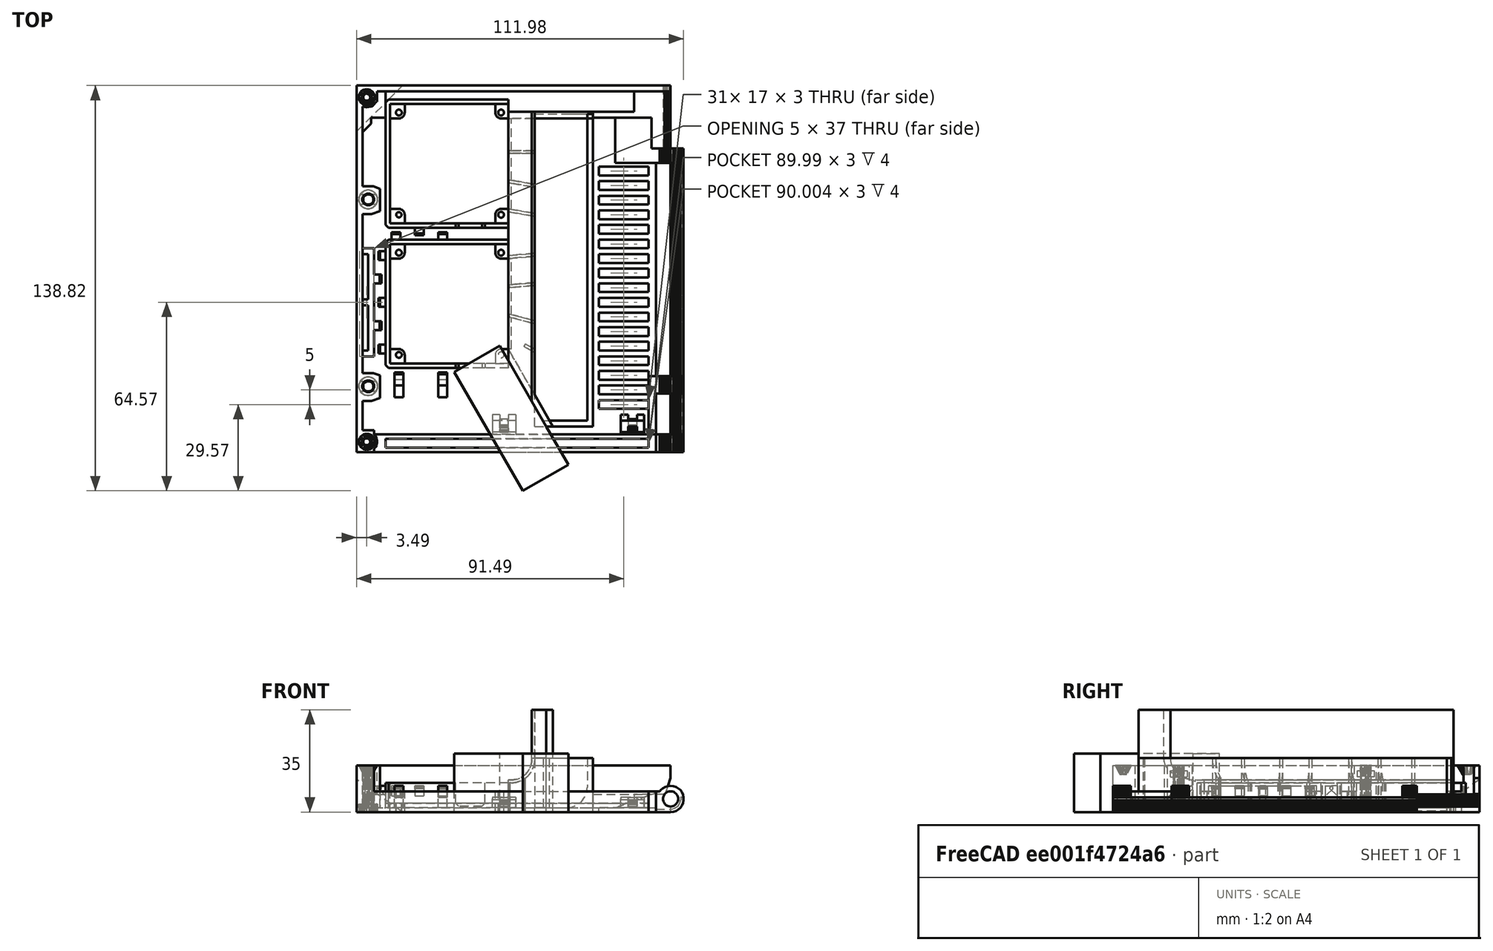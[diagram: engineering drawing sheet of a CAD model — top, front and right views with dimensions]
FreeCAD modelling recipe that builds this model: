
FCSTD DOCUMENT  (FreeCAD 0.18R14555 (Git shallow))
Label: SKR-DOOR-FROM-TOP
License: All rights reserved
LicenseURL: http://en.wikipedia.org/wiki/All_rights_reserved
objects: Part::Box×52, Part::MultiFuse×22, Part::Cut×21, Part::Feature×20, Part::Cylinder×8, Part::Chamfer×6, Part::Fillet×2, Mesh::Feature×1, Part::MultiCommon×1
note: 132 computed .brp shape members not serialized (recipe doc carries the construction recipe); baked Part::Feature solids carry a one-line shape summary decoded from their .brp

FEATURE [Mesh::Feature] SKR_13_DOOR_1_  label="SKR_13_DOOR(1)"
FEATURE [Part::Feature] Fusion001
  shape: bbox 112 x 125.5 x 16 mm, 668 faces (baked)
FEATURE [Part::Feature] Cut001_solid  label="4010-blower"
  Placement = pos=(-24,-12,0) rot=(0,0,1;3.14159rad)
  shape: bbox 42 x 44 x 10 mm, 38 faces (baked)
FEATURE [Part::Feature] Cut001_solid001  label="4010-blower001"
  Placement = pos=(-24,36,0) rot=(0,0,1;3.14159rad)
  shape: bbox 42 x 44 x 10 mm, 38 faces (baked)
FEATURE [Part::Box] Box002  label="Cube002"
  AttacherType = Attacher::AttachEngine3D
  Height = 10
  Length = 42
  Placement = pos=(-46,-6,0) rot=(0,0,1;0rad)
  Width = 44
FEATURE [Part::Box] Box003  label="Cube003"
  AttacherType = Attacher::AttachEngine3D
  Height = 10
  Length = 42
  Placement = pos=(-46,-54,0) rot=(0,0,1;0rad)
  Width = 44
FEATURE [Part::Chamfer] Chamfer
  Base = -> Box003
  Edges = 2 edges r=1.2: [Edge1,Edge3]
  Placement = pos=(0,20,0) rot=(0,0,1;0rad)
FEATURE [Part::Chamfer] Chamfer001
  Base = -> Box002
  Edges = 2 edges r=1.2: [Edge1,Edge3]
  Placement = pos=(0,20,0) rot=(0,0,1;0rad)
FEATURE [Part::Feature] Part__Feature  label="wire-mounter"
  Placement = pos=(-24,-80,64.25) rot=(-1,0,0;1.5708rad)
  shape: bbox 8 x 9.5 x 3.5 mm, 30 faces (baked)
FEATURE [Part::Feature] Part__Feature002  label="wire-mounter002"
  Placement = pos=(20,-80,64.25) rot=(-1,0,0;1.5708rad)
  shape: bbox 8 x 9.5 x 3.5 mm, 30 faces (baked)
FEATURE [Part::Feature] Chamfer003001  label="Chamfer004"
  Placement = pos=(-28,9,0) rot=(0,0,1;0rad)
  shape: bbox 3 x 3.5 x 4 mm, 8 faces (baked)
FEATURE [Part::Feature] Chamfer003002  label="Chamfer005"
  Placement = pos=(-44,9,0) rot=(0,0,1;0rad)
  shape: bbox 3 x 3.5 x 4 mm, 8 faces (baked)
FEATURE [Part::Feature] Chamfer003003  label="Chamfer006"
  Placement = pos=(-33,15,0) rot=(0,0,1;3.14159rad)
  shape: bbox 3 x 3.5 x 4 mm, 8 faces (baked)
FEATURE [Part::MultiFuse] Fusion002
  Shapes = -> [Cut001_solid001,Chamfer003003]
FEATURE [Part::MultiFuse] Fusion003
  Shapes = -> [Cut001_solid,Chamfer003001]
FEATURE [Part::MultiFuse] Fusion004
  Shapes = -> [Fusion003,Chamfer003002]
FEATURE [Part::Cut] Cut
  Base = -> Fusion001
  Tool = -> Chamfer001
FEATURE [Part::Cut] Cut001
  Base = -> Cut
  Tool = -> Chamfer
FEATURE [Part::Box] Box005  label="Cube005"
  AttacherType = Attacher::AttachEngine3D
  Height = 9
  Length = 2
  Placement = pos=(-52,-30,0) rot=(0,0,1;0rad)
  Width = 37
FEATURE [Part::Feature] Chamfer003005  label="wire-clip002"
  Placement = pos=(-45,-13,0) rot=(0,0,1;1.5708rad)
  shape: bbox 3.5 x 3 x 4 mm, 8 faces (baked)
FEATURE [Part::Feature] Chamfer003006  label="wire-clip003"
  Placement = pos=(-51,-2,0) rot=(0,0,-1;1.5708rad)
  shape: bbox 3.5 x 3 x 4 mm, 8 faces (baked)
FEATURE [Part::Feature] Chamfer003007  label="wire-clip004"
  Placement = pos=(-51,-18,0) rot=(0,0,-1;1.5708rad)
  shape: bbox 3.5 x 3 x 4 mm, 8 faces (baked)
FEATURE [Part::Feature] Chamfer003008  label="wire-clip005"
  Placement = pos=(-45,-29,0) rot=(0,0,1;1.5708rad)
  shape: bbox 3.5 x 3 x 4 mm, 8 faces (baked)
FEATURE [Part::Feature] Chamfer003009  label="wire-clip006"
  Placement = pos=(-45,3,0) rot=(0,0,1;1.5708rad)
  shape: bbox 3.5 x 3 x 4 mm, 8 faces (baked)
FEATURE [Part::Box] Box006  label="Cube006"
  AttacherType = Attacher::AttachEngine3D
  Height = 9
  Length = 4
  Placement = pos=(-55,-30,0) rot=(0,0,1;0rad)
  Width = 2
FEATURE [Part::Box] Box007  label="Cube007"
  AttacherType = Attacher::AttachEngine3D
  Height = 9
  Length = 4
  Placement = pos=(-55,5,0) rot=(0,0,1;0rad)
  Width = 2
FEATURE [Part::Box] Box008  label="Cube008"
  AttacherType = Attacher::AttachEngine3D
  Height = 9
  Length = 4
  Placement = pos=(-55,-12.5,0) rot=(0,0,1;0rad)
  Width = 2
FEATURE [Part::MultiFuse] Fusion006
  Shapes = -> [Fusion004,Chamfer003009,Chamfer003005,Chamfer003008]
FEATURE [Part::Box] Box009  label="Cube009"
  AttacherType = Attacher::AttachEngine3D
  Height = 9
  Length = 3
  Placement = pos=(-43,-40,0) rot=(0,0,1;0rad)
  Width = 2
FEATURE [Part::Box] Box010  label="Cube010"
  AttacherType = Attacher::AttachEngine3D
  Height = 9
  Length = 3
  Placement = pos=(-12,-40,0) rot=(0,0,1;0rad)
  Width = 2
FEATURE [Part::Feature] Chamfer003010  label="wire-clip007"
  Placement = pos=(-43,-39,0) rot=(0,0,1;0rad)
  shape: bbox 3 x 3.5 x 4 mm, 8 faces (baked)
FEATURE [Part::Feature] Chamfer003011  label="wire-clip008"
  Placement = pos=(-12,-39,0) rot=(0,0,1;0rad)
  shape: bbox 3 x 3.5 x 4 mm, 8 faces (baked)
FEATURE [Part::Box] Box011  label="Cube011"
  AttacherType = Attacher::AttachEngine3D
  Height = 9
  Length = 3
  Placement = pos=(-43,-44,0) rot=(0,0,1;0rad)
  Width = 6
FEATURE [Part::Box] Box012  label="Cube012"
  AttacherType = Attacher::AttachEngine3D
  Height = 9
  Length = 3
  Placement = pos=(-36,-44,0) rot=(0,0,1;0rad)
  Width = 6
FEATURE [Part::Chamfer] Chamfer003014
  Base = -> Box011
  Edges = 1 edges r=4: [Edge10]
FEATURE [Part::Chamfer] Chamfer003015
  Base = -> Box012
  Edges = 1 edges r=4: [Edge10]
  Placement = pos=(24,0,0) rot=(0,0,1;0rad)
FEATURE [Part::MultiFuse] Fusion007
  Shapes = -> [Box007,Box005,Box006,Box008,Chamfer003006,Chamfer003007]
FEATURE [Part::MultiFuse] Fusion008
  Shapes = -> [Chamfer003014,Chamfer003010,Box009]
FEATURE [Part::MultiFuse] Fusion009
  Placement = pos=(-16,0,0) rot=(0,0,1;0rad)
  Shapes = -> [Box010,Chamfer003011,Chamfer003015]
FEATURE [Part::MultiFuse] Fusion010
  Shapes = -> [Cut001,Fusion007]
FEATURE [Part::MultiFuse] Fusion011
  Shapes = -> [Fusion010,Fusion009]
FEATURE [Part::MultiFuse] Fusion012
  Shapes = -> [Fusion011,Fusion008]
FEATURE [Part::Cylinder] Cylinder  label="screw-hole-1"
  Angle = 360
  AttacherType = Attacher::AttachEngine3D
  Height = 10
  Placement = pos=(-41.5,5.5,0) rot=(0,0,1;0rad)
  Radius = 1
FEATURE [Part::Cylinder] Cylinder001  label="screw-hole-2"
  Angle = 360
  AttacherType = Attacher::AttachEngine3D
  Height = 10
  Placement = pos=(-41.5,18.5,0) rot=(0,0,1;0rad)
  Radius = 0.9
FEATURE [Part::Cylinder] Cylinder002  label="screw-hole-003"
  Angle = 360
  AttacherType = Attacher::AttachEngine3D
  Height = 10
  Placement = pos=(-6.5,-29.5,0) rot=(0,0,1;0rad)
  Radius = 1
FEATURE [Part::Cylinder] Cylinder003  label="screw-hole-004"
  Angle = 360
  AttacherType = Attacher::AttachEngine3D
  Height = 10
  Placement = pos=(-41.5,53.5,0) rot=(0,0,1;0rad)
  Radius = 1
FEATURE [Part::Cylinder] Cylinder004  label="screw-hole-005"
  Angle = 360
  AttacherType = Attacher::AttachEngine3D
  Height = 10
  Placement = pos=(-6.5,5.5,0) rot=(0,0,1;0rad)
  Radius = 1
FEATURE [Part::Cylinder] Cylinder005  label="screw-hole-006"
  Angle = 360
  AttacherType = Attacher::AttachEngine3D
  Height = 10
  Placement = pos=(-6.5,53.5,0) rot=(0,0,1;0rad)
  Radius = 1
FEATURE [Part::Cylinder] Cylinder006  label="screw-hole-007"
  Angle = 360
  AttacherType = Attacher::AttachEngine3D
  Height = 10
  Placement = pos=(-41.5,-29.5,0) rot=(0,0,1;0rad)
  Radius = 1
FEATURE [Part::Cylinder] Cylinder007  label="screw-hole-008"
  Angle = 360
  AttacherType = Attacher::AttachEngine3D
  Height = 10
  Placement = pos=(-6.5,18.5,0) rot=(0,0,1;0rad)
  Radius = 1
FEATURE [Part::Cut] Cut002
  Base = -> Fusion002
  Tool = -> Cylinder001
FEATURE [Part::Cut] Cut003
  Base = -> Cut002
  Tool = -> Cylinder007
FEATURE [Part::Cut] Cut004
  Base = -> Cut003
  Tool = -> Cylinder003
FEATURE [Part::Cut] Cut005
  Base = -> Cut004
  Tool = -> Cylinder005
FEATURE [Part::Cut] Cut006
  Base = -> Fusion006
  Tool = -> Cylinder006
FEATURE [Part::Cut] Cut007
  Base = -> Cut006
  Tool = -> Cylinder002
FEATURE [Part::Cut] Cut008
  Base = -> Cut007
  Tool = -> Cylinder
FEATURE [Part::Cut] Cut009
  Base = -> Cut008
  Tool = -> Cylinder004
FEATURE [Part::MultiFuse] Fusion013
  Shapes = -> [Fusion012,Cut009]
FEATURE [Part::MultiFuse] Fusion014  label="dorr-base"
  Shapes = -> [Cut005,Fusion013]
FEATURE [Part::Box] Box052  label="Cube050"
  AttacherType = Attacher::AttachEngine3D
  Height = 35
  Length = 14
  Placement = pos=(-5.75882,-15.9659,0) rot=(0,0,-1;0.261799rad)
  Width = 1
FEATURE [Part::Box] Box053  label="Cube051"
  AttacherType = Attacher::AttachEngine3D
  Height = 35
  Length = 36
  Placement = pos=(-6.99679,-26.3636,0) rot=(0,0,-1;1.0472rad)
  Width = 2
FEATURE [Part::Box] Box081  label="Cube079"
  AttacherType = Attacher::AttachEngine3D
  Height = 10
  Length = 17
  Placement = pos=(30,-43,0) rot=(0,0,1;0rad)
  Width = 3
FEATURE [Part::Box] Box082  label="Cube080"
  AttacherType = Attacher::AttachEngine3D
  Height = 10
  Length = 17
  Placement = pos=(30,-38,0) rot=(0,0,1;0rad)
  Width = 3
FEATURE [Part::Box] Box083  label="Cube081"
  AttacherType = Attacher::AttachEngine3D
  Height = 10
  Length = 17
  Placement = pos=(30,-28,0) rot=(0,0,1;0rad)
  Width = 3
FEATURE [Part::Box] Box084  label="Cube082"
  AttacherType = Attacher::AttachEngine3D
  Height = 10
  Length = 17
  Placement = pos=(30,-33,0) rot=(0,0,1;0rad)
  Width = 3
FEATURE [Part::Box] Box085  label="Cube083"
  AttacherType = Attacher::AttachEngine3D
  Height = 10
  Length = 17
  Placement = pos=(30,-23,0) rot=(0,0,1;0rad)
  Width = 3
FEATURE [Part::Box] Box086  label="Cube084"
  AttacherType = Attacher::AttachEngine3D
  Height = 10
  Length = 17
  Placement = pos=(30,-18,0) rot=(0,0,1;0rad)
  Width = 3
FEATURE [Part::Box] Box087  label="Cube085"
  AttacherType = Attacher::AttachEngine3D
  Height = 10
  Length = 17
  Placement = pos=(30,-13,0) rot=(0,0,1;0rad)
  Width = 3
FEATURE [Part::Box] Box088  label="Cube086"
  AttacherType = Attacher::AttachEngine3D
  Height = 10
  Length = 17
  Placement = pos=(30,-8,0) rot=(0,0,1;0rad)
  Width = 3
FEATURE [Part::Box] Box089  label="Cube087"
  AttacherType = Attacher::AttachEngine3D
  Height = 10
  Length = 17
  Placement = pos=(30,-3,0) rot=(0,0,1;0rad)
  Width = 3
FEATURE [Part::Box] Box090  label="Cube088"
  AttacherType = Attacher::AttachEngine3D
  Height = 10
  Length = 17
  Placement = pos=(30,2,0) rot=(0,0,1;0rad)
  Width = 3
FEATURE [Part::Box] Box091  label="Cube089"
  AttacherType = Attacher::AttachEngine3D
  Height = 10
  Length = 17
  Placement = pos=(30,7,0) rot=(0,0,1;0rad)
  Width = 3
FEATURE [Part::Box] Box092  label="Cube090"
  AttacherType = Attacher::AttachEngine3D
  Height = 10
  Length = 17
  Placement = pos=(30,12,0) rot=(0,0,1;0rad)
  Width = 3
FEATURE [Part::Box] Box093  label="Cube091"
  AttacherType = Attacher::AttachEngine3D
  Height = 10
  Length = 17
  Placement = pos=(30,17,0) rot=(0,0,1;0rad)
  Width = 3
FEATURE [Part::Box] Box094  label="Cube092"
  AttacherType = Attacher::AttachEngine3D
  Height = 10
  Length = 17
  Placement = pos=(30,27,0) rot=(0,0,1;0rad)
  Width = 3
FEATURE [Part::Box] Box095  label="Cube093"
  AttacherType = Attacher::AttachEngine3D
  Height = 10
  Length = 17
  Placement = pos=(30,22,0) rot=(0,0,1;0rad)
  Width = 3
FEATURE [Part::Box] Box096  label="Cube094"
  AttacherType = Attacher::AttachEngine3D
  Height = 10
  Length = 17
  Placement = pos=(30,32,0) rot=(0,0,1;0rad)
  Width = 3
FEATURE [Part::Box] Box098  label="trim-a001"
  AttacherType = Attacher::AttachEngine3D
  Height = 38
  Length = 35
  Placement = pos=(-20.8532,-34.3636,0) rot=(0,0,-1;1.0472rad)
  Width = 16
FEATURE [Part::Box] Box099  label="Cube095"
  AttacherType = Attacher::AttachEngine3D
  Height = 35
  Length = 10
  Placement = pos=(1.36603,-26.634,0) rot=(0,0,-1;0.523599rad)
  Width = 1
FEATURE [Part::Box] Box100  label="Cube096"
  AttacherType = Attacher::AttachEngine3D
  Height = 35
  Length = 13
  Placement = pos=(-5.49429,3.36927,0) rot=(0,0,1;0.087266rad)
  Width = 1
FEATURE [Part::Box] Box101  label="Cube097"
  AttacherType = Attacher::AttachEngine3D
  Height = 35
  Length = 15
  Placement = pos=(-5.72341,19.8039,0) rot=(0,0,-1;0.174533rad)
  Width = 1
FEATURE [Part::Box] Box102  label="Cube098"
  AttacherType = Attacher::AttachEngine3D
  Height = 35
  Length = 16
  Placement = pos=(-6.24144,-6.6961,0) rot=(0,0,1;0.087266rad)
  Width = 1
FEATURE [Part::Box] Box103  label="Cube099"
  AttacherType = Attacher::AttachEngine3D
  Height = 35
  Length = 13
  Placement = pos=(-4.73861,29.6302,0) rot=(0,0,-1;0.174533rad)
  Width = 1
FEATURE [Part::Box] Box104  label="Cube100"
  AttacherType = Attacher::AttachEngine3D
  Height = 35
  Length = 10
  Placement = pos=(-4,39.5,0) rot=(0,0,1;0rad)
  Width = 1
FEATURE [Part::Box] Box105  label="Cube101"
  AttacherType = Attacher::AttachEngine3D
  Height = 35
  Length = 40
  Placement = pos=(-4,51.5,0) rot=(0,0,1;0rad)
  Width = 2.25
FEATURE [Part::Box] Box107  label="Cube103"
  AttacherType = Attacher::AttachEngine3D
  Height = 43
  Length = 10
  Placement = pos=(5,-41,0) rot=(0,0,1;0rad)
  Width = 92
FEATURE [Part::Box] Box108  label="trim-a002"
  AttacherType = Attacher::AttachEngine3D
  Height = 20
  Length = 47
  Placement = pos=(-22.5852,-35.3636,0) rot=(0,0,-1;1.0472rad)
  Width = 18
FEATURE [Part::Box] Box111  label="Cube106"
  AttacherType = Attacher::AttachEngine3D
  Height = 10
  Length = 17
  Placement = pos=(30,-48,0) rot=(0,0,1;0rad)
  Width = 3
FEATURE [Part::Chamfer] Chamfer003019
  Base = -> Fusion014
  Edges = 2 edges r=1: [Edge106,Edge143]
FEATURE [Part::MultiFuse] Fusion018010
  Shapes = -> [Box053,Box052,Box101,Box103,Box100,Box102,Box104,Box105,Box099]
FEATURE [Part::Cut] Cut019
  Base = -> Fusion018010
  Tool = -> Box107
FEATURE [Part::Box] Box112  label="Cube107"
  AttacherType = Attacher::AttachEngine3D
  Height = 40
  Length = 10
  Placement = pos=(-14,-34,0) rot=(0,0,1;0rad)
  Width = 120
FEATURE [Part::Cut] Cut020
  Base = -> Cut019
  Tool = -> Box112
FEATURE [Part::Chamfer] Chamfer003020
  Base = -> Cut020
  Edges = 4 edges r=0.5: [Edge16,Edge40,Edge64,Edge75]
FEATURE [Part::Box] Box114  label="Cube109"
  AttacherType = Attacher::AttachEngine3D
  Height = 30
  Length = 9
  Placement = pos=(-4,-54,10) rot=(0,0,1;0rad)
  Width = 107.75
FEATURE [Part::Feature] Fillet002002001  label="Fillet002003"
  shape: bbox 9 x 107.8 x 25 mm, 10 faces (baked)
FEATURE [Part::Fillet] Fillet002002002
  Base = -> Box114
  Edges = 1 edges r=7: [Edge8]
  Placement = pos=(0,0,1) rot=(0,0,1;0rad)
FEATURE [Part::Cut] Cut022
  Base = -> Fillet002002001
  Tool = -> Box098
FEATURE [Part::Box] Box116  label="Cube111"
  AttacherType = Attacher::AttachEngine3D
  Height = 1.5
  Length = 20
  Placement = pos=(5,-54,0) rot=(0,0,1;0rad)
  Width = 107
FEATURE [Part::Box] Box117  label="Cube112"
  AttacherType = Attacher::AttachEngine3D
  Height = 18.5
  Length = 2
  Placement = pos=(23,-54,0) rot=(0,0,1;0rad)
  Width = 107
FEATURE [Part::MultiFuse] Fusion018011
  Shapes = -> [Box116,Box117]
FEATURE [Part::Fillet] Fillet002002003
  Base = -> Fusion018011
  Edges = 1 edges r=7: [Edge9]
FEATURE [Part::Box] Box118  label="Cube113"
  AttacherType = Attacher::AttachEngine3D
  Height = 41
  Length = 16
  Placement = pos=(0,-64,0) rot=(0,0,1;0rad)
  Width = 10
FEATURE [Part::Box] Box119  label="Cube114"
  AttacherType = Attacher::AttachEngine3D
  Height = 18.5
  Length = 17
  Placement = pos=(8,-54,0) rot=(0,0,1;0rad)
  Width = 2
FEATURE [Part::Cut] Cut025
  Base = -> Box119
  Tool = -> Box108
FEATURE [Part::MultiFuse] Fusion018012
  Shapes = -> [Cut025,Fillet002002003]
FEATURE [Part::Box] Box120  label="Cube115"
  AttacherType = Attacher::AttachEngine3D
  Height = 38
  Length = 14
  Placement = pos=(25,46,0) rot=(0,0,1;0rad)
  Width = 14
FEATURE [Part::Box] Box121  label="trim-a003"
  AttacherType = Attacher::AttachEngine3D
  Height = 20
  Length = 47
  Placement = pos=(-22.5852,-35.3636,0) rot=(0,0,-1;1.0472rad)
  Width = 18
FEATURE [Part::Box] Box122  label="Cube116"
  AttacherType = Attacher::AttachEngine3D
  Height = 19
  Length = 23
  Placement = pos=(5,45,18.5) rot=(0,0,1;0rad)
  Width = 14
FEATURE [Part::MultiFuse] Fusion018013
  Placement = pos=(-3,0,0) rot=(0,0,1;0rad)
  Shapes = -> [Box111,Box086,Box085,Box083,Box088,Box087,Box081,Box092,Box093,Box082,Box094,Box084,Box089,Box091,Box090,Box096,Box095]
FEATURE [Part::Cut] Cut028
  Base = -> Chamfer003019
  Tool = -> Fusion018013
FEATURE [Part::Box] Box123  label="Cube117"
  AttacherType = Attacher::AttachEngine3D
  Height = 18
  Length = 17
  Placement = pos=(0,-68,18.5) rot=(0,0,1;0rad)
  Width = 130
FEATURE [Part::Cut] Cut029
  Base = -> Chamfer003020
  Tool = -> Fillet002002002
FEATURE [Part::MultiFuse] Fusion
  Shapes = -> [Cut022,Cut029]
FEATURE [Part::Cut] Cut030
  Base = -> Fusion
  Tool = -> Box122
FEATURE [Part::Cut] Cut031
  Base = -> Cut030
  Tool = -> Box118
FEATURE [Part::Cut] Cut032
  Base = -> Cut031
  Tool = -> Box120
FEATURE [Part::Feature] Cut032001  label="Cut033"
  shape: bbox 29 x 107.8 x 35 mm, 55 faces (baked)
FEATURE [Part::Feature] Fusion018012001  label="Fusion018014"
  shape: bbox 20 x 107 x 18.5 mm, 12 faces (baked)
FEATURE [Part::Cut] Cut032002
  Base = -> Cut032001
  Tool = -> Box123
FEATURE [Part::MultiFuse] Fusion018012002
  Shapes = -> [Cut032002,Cut028]
FEATURE [Part::MultiFuse] Fusion018012003
  Shapes = -> [Fusion018012002,Fusion018012001]
FEATURE [Part::MultiFuse] Fusion018012004
  Shapes = -> [Fusion018012003,Part__Feature]
FEATURE [Part::MultiFuse] Fusion018012005  label="door-rev-3"
  Shapes = -> [Fusion018012004,Part__Feature002]
FEATURE [Part::Box] Box  label="Cube"
  AttacherType = Attacher::AttachEngine3D
  Height = 10
  Length = 12
  Placement = pos=(46.51,-62.75,0) rot=(0,0,1;0rad)
  Width = 20
FEATURE [Part::Feature] Fusion018012005001  label="door-rev-004"
  shape: bbox 112 x 125.5 x 18.5 mm, 1103 faces (baked)
FEATURE [Part::Feature] Fusion018012005002  label="door-rev-005"
  shape: bbox 112 x 125.5 x 18.5 mm, 1103 faces (baked)
FEATURE [Part::Box] Box124  label="Cube118"
  AttacherType = Attacher::AttachEngine3D
  Height = 10
  Length = 12
  Placement = pos=(46.51,-62.75,0) rot=(0,0,1;0rad)
  Width = 40
FEATURE [Part::MultiCommon] Common
  Placement = pos=(0,20,0) rot=(0,0,1;0rad)
  Shapes = -> [Fusion018012005001,Box]
FEATURE [Part::Cut] Cut032003
  Base = -> Fusion018012005002
  Tool = -> Box124
FEATURE [Part::Box] Box125  label="Cube119"
  AttacherType = Attacher::AttachEngine3D
  Height = 7
  Length = 2.51
  Placement = pos=(44,-62.75,0) rot=(0,0,1;0rad)
  Width = 26
FEATURE [Part::MultiFuse] Fusion018012005003  label="prusa-door-rev3"
  Shapes = -> [Box125,Cut032003,Common]
